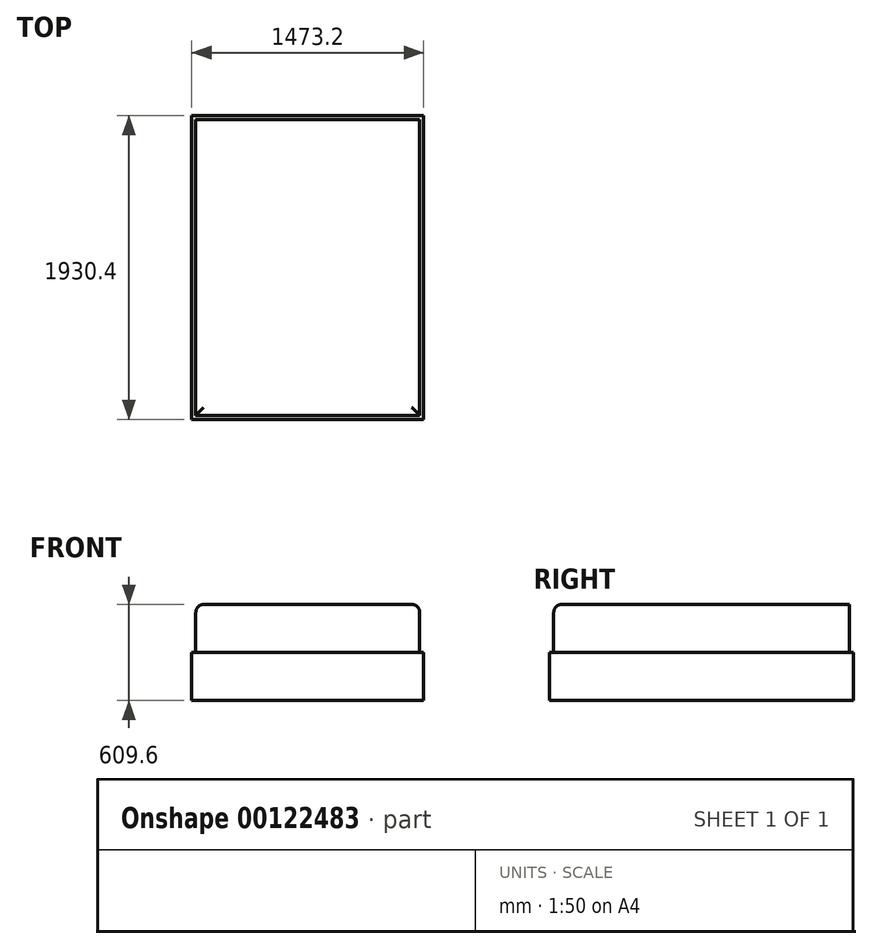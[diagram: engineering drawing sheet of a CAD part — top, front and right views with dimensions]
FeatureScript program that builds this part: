
annotation { "Feature Type Name" : "Feature", "Feature Type Description" : "" }
export const myFeature = defineFeature(function(context is Context, id is Id, definition is map)
    precondition{}
    {
        {
            var Q0;
            Q0=qCreatedBy(makeId("Top.planeOp"),FACE);
            var sketch = newSketch(context, id + "F0", { "sketchPlane" : qUnion([Q0])});
            skLineSegment(sketch, "E0.bottom", {"start": v(0, 0) * mm, "end": v(-1422.4, 0) * mm});
            skLineSegment(sketch, "E0.top", {"start": v(0, 1879.6) * mm, "end": v(-1422.4, 1879.6) * mm});
            skLineSegment(sketch, "E0.left", {"start": v(0, 0) * mm, "end": v(0, 1879.6) * mm});
            skLineSegment(sketch, "E0.right", {"start": v(-1422.4, 0) * mm, "end": v(-1422.4, 1879.6) * mm});
            skSolve(sketch);
        }
        {
            var Q0;
            Q0=qSketchRegion(id+"F0",true);
            extrude(context, id + "F1", {"entities" : qUnion([Q0]), "depth" : 609.6 * mm});
        }
        {
            var Q0;
            Q0=makeQuery(id+"F1.opExtrude","CAP_EDGE",EDGE,{"disambiguationData":[OSD([sQuery(id+"F0.wireOp",EDGE,"E0.bottom")])],"isStart":false});
            var Q1;
            Q1=makeQuery(id+"F1.opExtrude","CAP_EDGE",EDGE,{"disambiguationData":[OSD([sQuery(id+"F0.wireOp",EDGE,"E0.right")])],"isStart":false});
            var Q2;
            Q2=makeQuery(id+"F1.opExtrude","CAP_EDGE",EDGE,{"disambiguationData":[OSD([sQuery(id+"F0.wireOp",EDGE,"E0.left")])],"isStart":false});
            fillet(context, id + "F2", {"entities" : qUnion([Q0, Q1, Q2]), "radius" : 50.8 * mm, "tangentPropagation" : true, "allowEdgeOverflow" : false});
        }
        {
            var Q0;
            Q0=qCreatedBy(makeId("Top.planeOp"),FACE);
            var sketch = newSketch(context, id + "F3", { "sketchPlane" : qUnion([Q0])});
            skLineSegment(sketch, "E1.bottom", {"start": v(25.4, -25.4) * mm, "end": v(-1447.8, -25.4) * mm});
            skLineSegment(sketch, "E1.top", {"start": v(25.4, 1905) * mm, "end": v(-1447.8, 1905) * mm});
            skLineSegment(sketch, "E1.left", {"start": v(25.4, -25.4) * mm, "end": v(25.4, 1905) * mm});
            skLineSegment(sketch, "E1.right", {"start": v(-1447.8, -25.4) * mm, "end": v(-1447.8, 1905) * mm});
            skSolve(sketch);
        }
        {
            var Q0;
            Q0=qSketchRegion(id+"F3",true);
            extrude(context, id + "F4", {"entities" : qUnion([Q0]), "operationType" : NewBodyOperationType.ADD, "depth" : 304.8 * mm});
        }
    });
